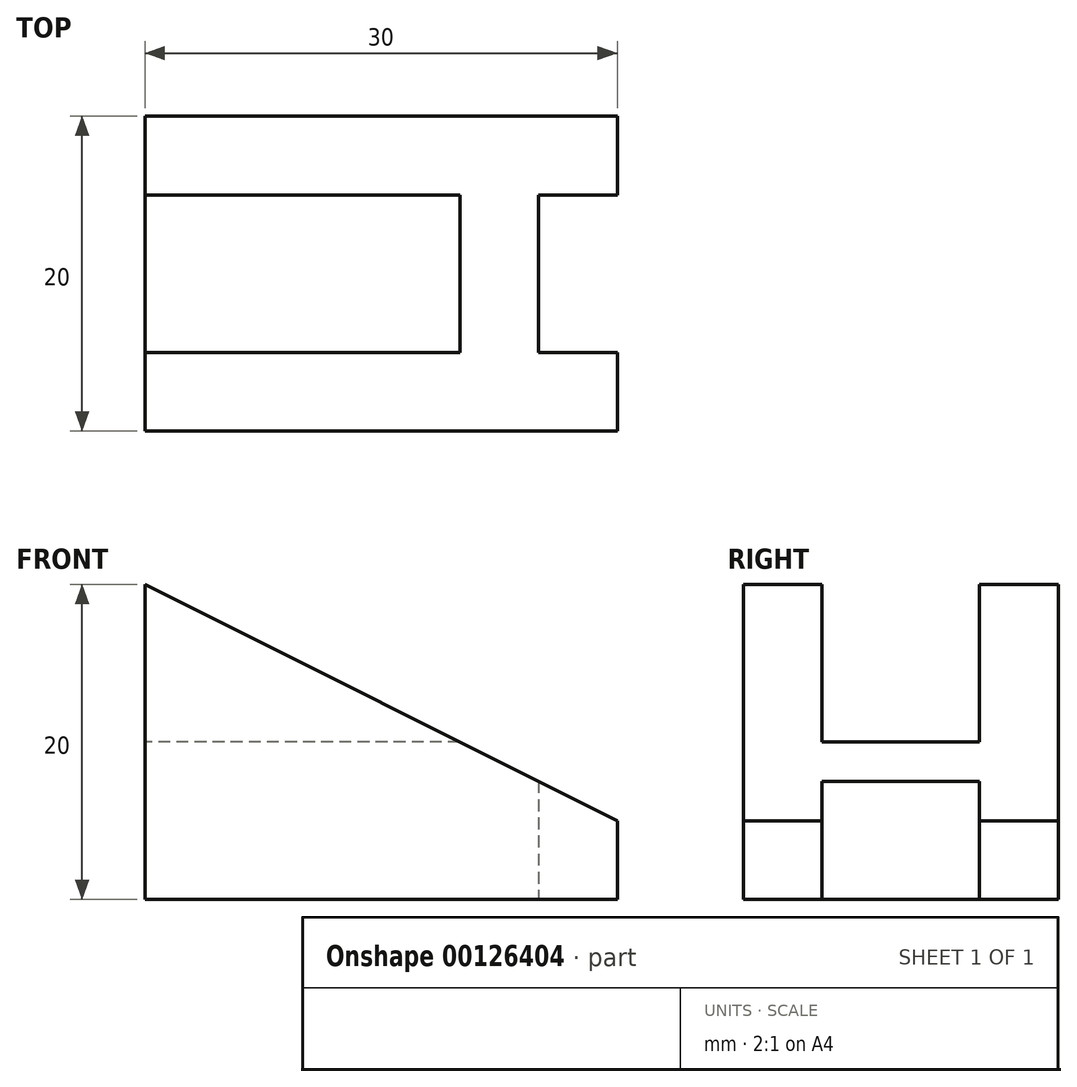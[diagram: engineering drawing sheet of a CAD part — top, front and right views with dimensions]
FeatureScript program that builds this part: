
annotation { "Feature Type Name" : "Feature", "Feature Type Description" : "" }
export const myFeature = defineFeature(function(context is Context, id is Id, definition is map)
    precondition{}
    {
        {
            var Q0;
            Q0=qCreatedBy(makeId("Right.planeOp"),FACE);
            var sketch = newSketch(context, id + "F0", { "sketchPlane" : qUnion([Q0])});
            skLineSegment(sketch, "E0", {"start": v(0, 0) * mm, "end": v(-10, 0) * mm});
            skLineSegment(sketch, "E1", {"start": v(-10, 0) * mm, "end": v(-10, 20) * mm});
            skLineSegment(sketch, "E2", {"start": v(-10, 20) * mm, "end": v(-5, 20) * mm});
            skLineSegment(sketch, "E3", {"start": v(-5, 20) * mm, "end": v(-5, 10) * mm});
            skLineSegment(sketch, "E4", {"start": v(-5, 10) * mm, "end": v(0, 10) * mm});
            skLineSegment(sketch, "E5.MirrorCS", {"start": v(10, 20) * mm, "end": v(5, 20) * mm});
            skLineSegment(sketch, "E6.MirrorCS", {"start": v(10, 0) * mm, "end": v(10, 20) * mm});
            skLineSegment(sketch, "E7.MirrorCS", {"start": v(5, 20) * mm, "end": v(5, 10) * mm});
            skLineSegment(sketch, "E8.MirrorCS", {"start": v(5, 10) * mm, "end": v(0, 10) * mm});
            skLineSegment(sketch, "E9.MirrorCS", {"start": v(0, 0) * mm, "end": v(10, 0) * mm});
            skSolve(sketch);
        }
        {
            var Q0;
            Q0=qSketchRegion(id+"F0",true);
            extrude(context, id + "F1", {"entities" : qUnion([Q0]), "endBound" : BoundingType.SYMMETRIC, "depth" : 30 * mm});
        }
        {
            var Q0;
            Q0=makeQuery(id+"F1.opExtrude","SWEPT_FACE",FACE,{"disambiguationData":[OSD([sQuery(id+"F0.wireOp",EDGE,"E1")])]});
            var sketch = newSketch(context, id + "F2", { "sketchPlane" : qUnion([Q0])});
            skLineSegment(sketch, "E10", {"start": v(-15, 20) * mm, "end": v(-15, 0) * mm});
            skLineSegment(sketch, "E11", {"start": v(-15, 0) * mm, "end": v(15, 0) * mm});
            skLineSegment(sketch, "E12", {"start": v(15, 0) * mm, "end": v(15, 5) * mm});
            skLineSegment(sketch, "E13", {"start": v(15, 5) * mm, "end": v(-15, 20) * mm});
            skSolve(sketch);
        }
        {
            var Q0;
            {var subQ0=sQuery(id+"F2.wireOp",EDGE,"E13");Q0=makeQuery(id+"F2.imprint","IMPRINT",FACE,{"disambiguationData":[TD([[makeQuery(id+"F2.imprint","IMPRINT",EDGE,{"derivedFrom":subQ0}),-1.0]])]});}
            extrude(context, id + "F3", {"entities" : qUnion([Q0]), "operationType" : NewBodyOperationType.REMOVE, "endBound" : BoundingType.THROUGH_ALL, "oppositeDirection" : true, "depth" : 25 * mm});
        }
        {
            var Q0;
            Q0=makeQuery(id+"F1.opExtrude","CAP_FACE",FACE,{"disambiguationData":[OSD([sQuery(id+"F0.wireOp",EDGE,"E0"),sQuery(id+"F0.wireOp",EDGE,"E1"),sQuery(id+"F0.wireOp",EDGE,"E2"),sQuery(id+"F0.wireOp",EDGE,"E3"),sQuery(id+"F0.wireOp",EDGE,"E4"),sQuery(id+"F0.wireOp",EDGE,"E5.MirrorCS"),sQuery(id+"F0.wireOp",EDGE,"E6.MirrorCS"),sQuery(id+"F0.wireOp",EDGE,"E7.MirrorCS"),sQuery(id+"F0.wireOp",EDGE,"E8.MirrorCS"),sQuery(id+"F0.wireOp",EDGE,"E9.MirrorCS")])],"isStart":false});
            var sketch = newSketch(context, id + "F4", { "sketchPlane" : qUnion([Q0])});
            skLineSegment(sketch, "E14.bottom", {"start": v(-5, 5) * mm, "end": v(5, 5) * mm});
            skLineSegment(sketch, "E14.top", {"start": v(-5, 0) * mm, "end": v(5, 0) * mm});
            skLineSegment(sketch, "E14.left", {"start": v(-5, 5) * mm, "end": v(-5, 0) * mm});
            skLineSegment(sketch, "E14.right", {"start": v(5, 5) * mm, "end": v(5, 0) * mm});
            skPoint(sketch, "E15", {"position": v(0, 5) * mm});
            skSolve(sketch);
        }
        {
            var Q0;
            Q0=makeQuery(id+"F4.imprint","IMPRINT",FACE,{"disambiguationData":[TD([[makeQuery(id+"F4.imprint","IMPRINT",EDGE,{"derivedFrom":sQuery(id+"F4.wireOp",EDGE,"E14.bottom")}),1.0]])]});
            extrude(context, id + "F5", {"entities" : qUnion([Q0]), "operationType" : NewBodyOperationType.REMOVE, "oppositeDirection" : true, "depth" : 5 * mm});
        }
        {
            var Q0;
            Q0=qCreatedBy(makeId("Top.planeOp"),FACE);
            var sketch = newSketch(context, id + "F6", { "sketchPlane" : qUnion([Q0])});
            skLineSegment(sketch, "E16", {"start": v(15, 0) * mm, "end": v(15, 5) * mm});
            skLineSegment(sketch, "E17", {"start": v(15, 5) * mm, "end": v(10, 5) * mm});
            skLineSegment(sketch, "E18", {"start": v(10, 5) * mm, "end": v(10, 0) * mm});
            skLineSegment(sketch, "E19.MirrorCS", {"start": v(15, -5) * mm, "end": v(10, -5) * mm});
            skLineSegment(sketch, "E20.MirrorCS", {"start": v(10, -5) * mm, "end": v(10, 0) * mm});
            skLineSegment(sketch, "E21.MirrorCS", {"start": v(15, 0) * mm, "end": v(15, -5) * mm});
            skSolve(sketch);
        }
        {
            var Q0;
            Q0=makeQuery(id+"F6.imprint","IMPRINT",FACE,{"disambiguationData":[TD([[makeQuery(id+"F6.imprint","IMPRINT",EDGE,{"derivedFrom":sQuery(id+"F6.wireOp",EDGE,"E16")}),1.0]])]});
            var Q1;
            Q1=sQuery(id+"F6.wireOp",EDGE,"E17");
            var Q2;
            Q2=sQuery(id+"F6.wireOp",EDGE,"E18");
            var Q3;
            Q3=sQuery(id+"F6.wireOp",EDGE,"E20.MirrorCS");
            var Q4;
            Q4=sQuery(id+"F6.wireOp",EDGE,"E19.MirrorCS");
            extrude(context, id + "F7", {"entities" : qUnion([Q0]), "operationType" : NewBodyOperationType.REMOVE, "surfaceEntities" : qUnion([Q1, Q2, Q3, Q4]), "endBound" : BoundingType.THROUGH_ALL, "depth" : 11.5 * mm});
        }
    });
